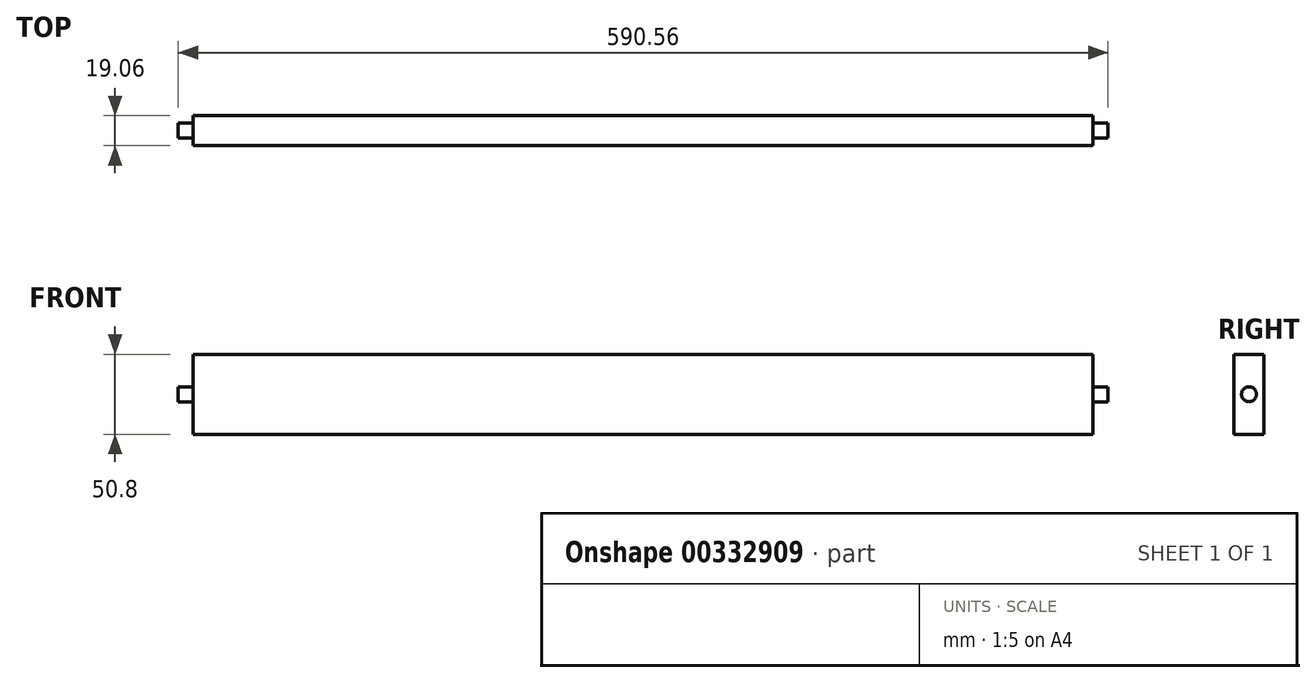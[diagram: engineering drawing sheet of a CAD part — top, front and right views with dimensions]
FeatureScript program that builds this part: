
annotation { "Feature Type Name" : "Feature", "Feature Type Description" : "" }
export const myFeature = defineFeature(function(context is Context, id is Id, definition is map)
    precondition{}
    {
        {
            var Q0;
            Q0=qCreatedBy(makeId("Right.planeOp"),FACE);
            var sketch = newSketch(context, id + "F0", { "sketchPlane" : qUnion([Q0])});
            skLineSegment(sketch, "E0.bottom", {"start": v(-9.52, -25.4) * mm, "end": v(9.53, -25.4) * mm});
            skLineSegment(sketch, "E0.top", {"start": v(-9.53, 25.4) * mm, "end": v(9.52, 25.4) * mm});
            skLineSegment(sketch, "E0.left", {"start": v(-9.52, -25.4) * mm, "end": v(-9.53, 25.4) * mm});
            skLineSegment(sketch, "E0.right", {"start": v(9.53, -25.4) * mm, "end": v(9.52, 25.4) * mm});
            skPoint(sketch, "E0.middle", {"position": v(0, 0) * mm});
            skSolve(sketch);
        }
        {
            var Q0;
            Q0 = qSketchRegion(id + "F0", true);
            extrude(context, id + "F1", {"entities" : qUnion([Q0]), "endBound" : BoundingType.SYMMETRIC, "depth" : 590.55 * mm});
        }
        {
            var Q0;
            Q0=qCreatedBy(makeId("Right.planeOp"),FACE);
            cPlane(context, id + "F2", {"entities" : qUnion([Q0]), "cplaneType" : CPlaneType.OFFSET, "offset" : 285.75 * mm, "width" : 152.4 * mm, "height" : 152.4 * mm});
        }
        {
            var Q0;
            Q0=qCreatedBy(id+"F2.planeOp",FACE);
            var sketch = newSketch(context, id + "F3", { "sketchPlane" : qUnion([Q0])});
            skCircle(sketch, "E1", {"center": v(0, 0) * mm, "radius": 4.76 * mm});
            skLineSegment(sketch, "E2.bottom", {"start": v(36.83, 35.08) * mm, "end": v(-36.83, 35.08) * mm});
            skLineSegment(sketch, "E2.top", {"start": v(36.83, -35.08) * mm, "end": v(-36.83, -35.08) * mm});
            skLineSegment(sketch, "E2.left", {"start": v(36.83, 35.08) * mm, "end": v(36.83, -35.08) * mm});
            skLineSegment(sketch, "E2.right", {"start": v(-36.83, 35.08) * mm, "end": v(-36.83, -35.08) * mm});
            skSolve(sketch);
        }
        {
            var Q0;
            Q0 = qSketchRegion(id + "F3", true);
            extrude(context, id + "F4", {"entities" : qUnion([Q0]), "operationType" : NewBodyOperationType.REMOVE, "endBound" : BoundingType.THROUGH_ALL, "depth" : 9.52 * mm});
        }
        {
            var Q0;
            Q0=qCreatedBy(makeId("Right.planeOp"),FACE);
            cPlane(context, id + "F5", {"entities" : qUnion([Q0]), "cplaneType" : CPlaneType.OFFSET, "offset" : 285.75 * mm, "oppositeDirection" : true, "width" : 152.4 * mm, "height" : 152.4 * mm});
        }
        {
            var Q0;
            Q0=qCreatedBy(id+"F5.planeOp",FACE);
            var sketch = newSketch(context, id + "F6", { "sketchPlane" : qUnion([Q0])});
            skCircle(sketch, "E3", {"center": v(0, 0) * mm, "radius": 4.76 * mm});
            skLineSegment(sketch, "E4.bottom", {"start": v(-29.94, -30.9) * mm, "end": v(29.94, -30.9) * mm});
            skLineSegment(sketch, "E4.top", {"start": v(-29.94, 30.9) * mm, "end": v(29.94, 30.9) * mm});
            skLineSegment(sketch, "E4.left", {"start": v(-29.94, -30.9) * mm, "end": v(-29.94, 30.9) * mm});
            skLineSegment(sketch, "E4.right", {"start": v(29.94, -30.9) * mm, "end": v(29.94, 30.9) * mm});
            skSolve(sketch);
        }
        {
            var Q0;
            Q0 = qSketchRegion(id + "F6", true);
            extrude(context, id + "F7", {"entities" : qUnion([Q0]), "operationType" : NewBodyOperationType.REMOVE, "oppositeDirection" : true, "depth" : 9.52 * mm});
        }
    });
